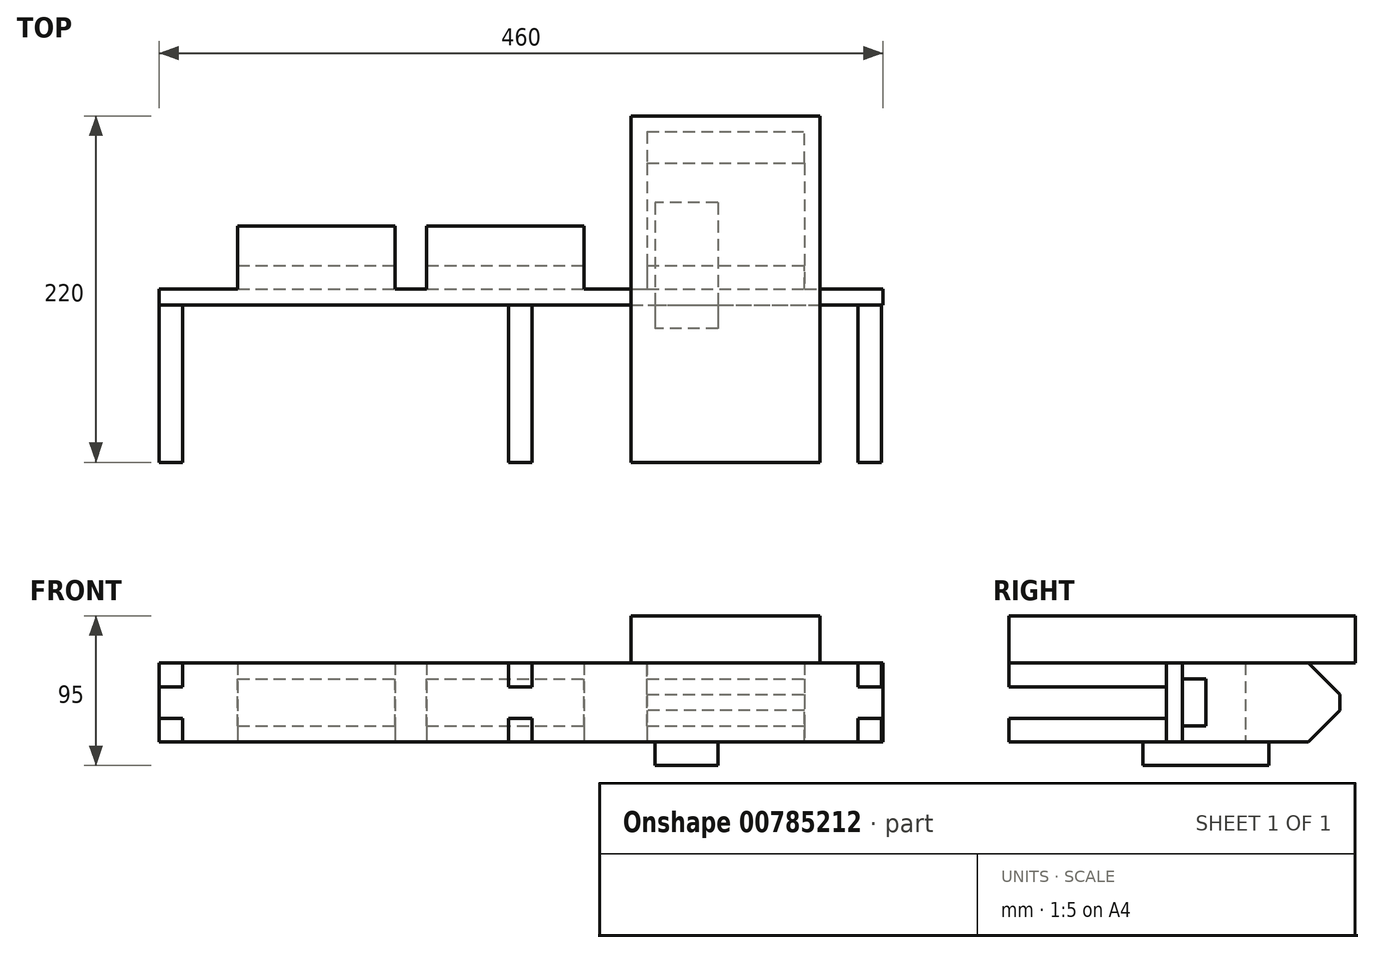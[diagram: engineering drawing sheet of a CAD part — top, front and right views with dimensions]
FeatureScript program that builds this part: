
annotation { "Feature Type Name" : "Feature", "Feature Type Description" : "" }
export const myFeature = defineFeature(function(context is Context, id is Id, definition is map)
    precondition{}
    {
        {
            var Q0;
            Q0=qCreatedBy(makeId("Front.planeOp"),FACE);
            var sketch = newSketch(context, id + "F0", { "sketchPlane" : qUnion([Q0])});
            skLineSegment(sketch, "E0.bottom", {"start": v(0, 0) * mm, "end": v(460, 0) * mm});
            skLineSegment(sketch, "E0.top", {"start": v(0, 50) * mm, "end": v(460, 50) * mm});
            skLineSegment(sketch, "E0.left", {"start": v(0, 0) * mm, "end": v(0, 50) * mm});
            skLineSegment(sketch, "E0.right", {"start": v(460, 0) * mm, "end": v(460, 50) * mm});
            skSolve(sketch);
        }
        {
            var Q0;
            Q0=makeQuery(id+"F0.imprint","IMPRINT",FACE,{"disambiguationData":[TD([[makeQuery(id+"F0.imprint","IMPRINT",EDGE,{"derivedFrom":sQuery(id+"F0.wireOp",EDGE,"E0.bottom")}),1.0]])]});
            extrude(context, id + "F1", {"entities" : qUnion([Q0]), "depth" : 10 * mm, "offsetDistance" : 25 * mm});
        }
        {
            var Q0;
            Q0=makeQuery(id+"F1.opExtrude","CAP_FACE",FACE,{"disambiguationData":[OSD([sQuery(id+"F0.wireOp",EDGE,"E0.bottom"),sQuery(id+"F0.wireOp",EDGE,"E0.top"),sQuery(id+"F0.wireOp",EDGE,"E0.left"),sQuery(id+"F0.wireOp",EDGE,"E0.right")])],"isStart":false});
            var sketch = newSketch(context, id + "F2", { "sketchPlane" : qUnion([Q0])});
            skLineSegment(sketch, "E1.bottom", {"start": v(0, 50) * mm, "end": v(15, 50) * mm});
            skLineSegment(sketch, "E1.top", {"start": v(0, 35) * mm, "end": v(15, 35) * mm});
            skLineSegment(sketch, "E1.left", {"start": v(0, 50) * mm, "end": v(0, 35) * mm});
            skLineSegment(sketch, "E1.right", {"start": v(15, 50) * mm, "end": v(15, 35) * mm});
            skLineSegment(sketch, "E2.bottom", {"start": v(0, 0) * mm, "end": v(15, 0) * mm});
            skLineSegment(sketch, "E2.top", {"start": v(0, 15) * mm, "end": v(15, 15) * mm});
            skLineSegment(sketch, "E2.left", {"start": v(0, 0) * mm, "end": v(0, 15) * mm});
            skLineSegment(sketch, "E2.right", {"start": v(15, 0) * mm, "end": v(15, 15) * mm});
            skLineSegment(sketch, "E3.1.0.0", {"start": v(222, 35) * mm, "end": v(237, 35) * mm});
            skLineSegment(sketch, "E3.1.0.1", {"start": v(222, 50) * mm, "end": v(237, 50) * mm});
            skLineSegment(sketch, "E3.1.0.2", {"start": v(222, 50) * mm, "end": v(222, 35) * mm});
            skLineSegment(sketch, "E3.1.0.3", {"start": v(237, 50) * mm, "end": v(237, 35) * mm});
            skLineSegment(sketch, "E3.1.0.4", {"start": v(222, 0) * mm, "end": v(237, 0) * mm});
            skLineSegment(sketch, "E3.1.0.5", {"start": v(222, 15) * mm, "end": v(237, 15) * mm});
            skLineSegment(sketch, "E3.1.0.6", {"start": v(222, 0) * mm, "end": v(222, 15) * mm});
            skLineSegment(sketch, "E3.1.0.7", {"start": v(237, 0) * mm, "end": v(237, 15) * mm});
            skLineSegment(sketch, "E3.2.0.0", {"start": v(444, 35) * mm, "end": v(459, 35) * mm});
            skLineSegment(sketch, "E3.2.0.1", {"start": v(444, 50) * mm, "end": v(459, 50) * mm});
            skLineSegment(sketch, "E3.2.0.2", {"start": v(444, 50) * mm, "end": v(444, 35) * mm});
            skLineSegment(sketch, "E3.2.0.3", {"start": v(459, 50) * mm, "end": v(459, 35) * mm});
            skLineSegment(sketch, "E3.2.0.4", {"start": v(444, 0) * mm, "end": v(459, 0) * mm});
            skLineSegment(sketch, "E3.2.0.5", {"start": v(444, 15) * mm, "end": v(459, 15) * mm});
            skLineSegment(sketch, "E3.2.0.6", {"start": v(444, 0) * mm, "end": v(444, 15) * mm});
            skLineSegment(sketch, "E3.2.0.7", {"start": v(459, 0) * mm, "end": v(459, 15) * mm});
            skLineSegment(sketch, "E3.direction1", {"start": v(0, 0) * mm, "end": v(222, 0) * mm, "construction": true});
            skSolve(sketch);
        }
        {
            var Q0;
            Q0=makeQuery(id+"F2.imprint","IMPRINT",FACE,{"disambiguationData":[TD([[makeQuery(id+"F2.imprint","IMPRINT",EDGE,{"derivedFrom":sQuery(id+"F2.wireOp",EDGE,"E1.bottom")}),-1.0]])]});
            var Q1;
            Q1=makeQuery(id+"F2.imprint","IMPRINT",FACE,{"disambiguationData":[TD([[makeQuery(id+"F2.imprint","IMPRINT",EDGE,{"derivedFrom":sQuery(id+"F2.wireOp",EDGE,"E2.bottom")}),1.0]])]});
            var Q2;
            Q2=makeQuery(id+"F2.imprint","IMPRINT",FACE,{"disambiguationData":[TD([[makeQuery(id+"F2.imprint","IMPRINT",EDGE,{"derivedFrom":sQuery(id+"F2.wireOp",EDGE,"E3.1.0.0")}),1.0]])]});
            var Q3;
            Q3=makeQuery(id+"F2.imprint","IMPRINT",FACE,{"disambiguationData":[TD([[makeQuery(id+"F2.imprint","IMPRINT",EDGE,{"derivedFrom":sQuery(id+"F2.wireOp",EDGE,"E3.1.0.4")}),1.0]])]});
            var Q4;
            Q4=makeQuery(id+"F2.imprint","IMPRINT",FACE,{"disambiguationData":[TD([[makeQuery(id+"F2.imprint","IMPRINT",EDGE,{"derivedFrom":sQuery(id+"F2.wireOp",EDGE,"E3.2.0.0")}),1.0]])]});
            var Q5;
            Q5=makeQuery(id+"F2.imprint","IMPRINT",FACE,{"disambiguationData":[TD([[makeQuery(id+"F2.imprint","IMPRINT",EDGE,{"derivedFrom":sQuery(id+"F2.wireOp",EDGE,"E3.2.0.4")}),1.0]])]});
            extrude(context, id + "F3", {"entities" : qUnion([Q0, Q1, Q2, Q3, Q4, Q5]), "depth" : 100 * mm, "offsetDistance" : 25 * mm});
        }
        {
            var Q0;
            Q0=makeQuery(id+"F1.opExtrude","CAP_FACE",FACE,{"disambiguationData":[OSD([sQuery(id+"F0.wireOp",EDGE,"E0.bottom"),sQuery(id+"F0.wireOp",EDGE,"E0.top"),sQuery(id+"F0.wireOp",EDGE,"E0.left"),sQuery(id+"F0.wireOp",EDGE,"E0.right")])],"isStart":true});
            var sketch = newSketch(context, id + "F4", { "sketchPlane" : qUnion([Q0])});
            skLineSegment(sketch, "E4.bottom", {"start": v(-410, 50) * mm, "end": v(-310, 50) * mm});
            skLineSegment(sketch, "E4.top", {"start": v(-410, 0) * mm, "end": v(-310, 0) * mm});
            skLineSegment(sketch, "E4.left", {"start": v(-410, 50) * mm, "end": v(-410, 0) * mm});
            skLineSegment(sketch, "E4.right", {"start": v(-310, 50) * mm, "end": v(-310, 0) * mm});
            skLineSegment(sketch, "E5.bottom", {"start": v(-270, 50) * mm, "end": v(-170, 50) * mm});
            skLineSegment(sketch, "E5.top", {"start": v(-270, 0) * mm, "end": v(-170, 0) * mm});
            skLineSegment(sketch, "E5.left", {"start": v(-270, 50) * mm, "end": v(-270, 0) * mm});
            skLineSegment(sketch, "E5.right", {"start": v(-170, 50) * mm, "end": v(-170, 0) * mm});
            skLineSegment(sketch, "E6.bottom", {"start": v(-150, 50) * mm, "end": v(-50, 50) * mm});
            skLineSegment(sketch, "E6.top", {"start": v(-150, 0) * mm, "end": v(-50, 0) * mm});
            skLineSegment(sketch, "E6.left", {"start": v(-150, 50) * mm, "end": v(-150, 0) * mm});
            skLineSegment(sketch, "E6.right", {"start": v(-50, 50) * mm, "end": v(-50, 0) * mm});
            skSolve(sketch);
        }
        {
            var Q0;
            Q0=makeQuery(id+"F4.imprint","IMPRINT",FACE,{"disambiguationData":[TD([[makeQuery(id+"F4.imprint","IMPRINT",EDGE,{"derivedFrom":sQuery(id+"F4.wireOp",EDGE,"E4.bottom")}),1.0]])]});
            var Q1;
            Q1=makeQuery(id+"F4.imprint","IMPRINT",FACE,{"disambiguationData":[TD([[makeQuery(id+"F4.imprint","IMPRINT",EDGE,{"derivedFrom":sQuery(id+"F4.wireOp",EDGE,"E5.bottom")}),1.0]])]});
            var Q2;
            Q2=makeQuery(id+"F4.imprint","IMPRINT",FACE,{"disambiguationData":[TD([[makeQuery(id+"F4.imprint","IMPRINT",EDGE,{"derivedFrom":sQuery(id+"F4.wireOp",EDGE,"E6.bottom")}),1.0]])]});
            extrude(context, id + "F5", {"entities" : qUnion([Q0, Q1, Q2]), "operationType" : NewBodyOperationType.ADD, "depth" : 40 * mm, "offsetDistance" : 25 * mm});
        }
        {
            var Q0;
            Q0=makeQuery(id+"F5.opExtrude","CAP_FACE",FACE,{"disambiguationData":[OSD([sQuery(id+"F4.wireOp",EDGE,"E4.bottom"),sQuery(id+"F4.wireOp",EDGE,"E4.top"),sQuery(id+"F4.wireOp",EDGE,"E4.left"),sQuery(id+"F4.wireOp",EDGE,"E4.right")])],"isStart":false});
            var sketch = newSketch(context, id + "F6", { "sketchPlane" : qUnion([Q0])});
            skLineSegment(sketch, "E7.bottom", {"start": v(-410, 50) * mm, "end": v(-310, 50) * mm});
            skLineSegment(sketch, "E7.top", {"start": v(-410, 0) * mm, "end": v(-310, 0) * mm});
            skLineSegment(sketch, "E7.left", {"start": v(-410, 50) * mm, "end": v(-410, 0) * mm});
            skLineSegment(sketch, "E7.right", {"start": v(-310, 50) * mm, "end": v(-310, 0) * mm});
            skSolve(sketch);
        }
        {
            var Q0;
            Q0=makeQuery(id+"F6.imprint","IMPRINT",FACE,{"disambiguationData":[TD([[makeQuery(id+"F6.imprint","IMPRINT",EDGE,{"derivedFrom":sQuery(id+"F6.wireOp",EDGE,"E7.bottom")}),1.0]])]});
            extrude(context, id + "F7", {"entities" : qUnion([Q0]), "operationType" : NewBodyOperationType.ADD, "depth" : 60 * mm, "offsetDistance" : 25 * mm});
        }
        {
            var Q0;
            Q0=makeQuery(id+"F7.opExtrude","CAP_EDGE",EDGE,{"disambiguationData":[OSD([sQuery(id+"F6.wireOp",EDGE,"E7.top")])],"isStart":false});
            var Q1;
            Q1=makeQuery(id+"F7.opExtrude","CAP_EDGE",EDGE,{"disambiguationData":[OSD([sQuery(id+"F6.wireOp",EDGE,"E7.bottom")])],"isStart":false});
            chamfer(context, id + "F8", {"entities" : qUnion([Q0, Q1]), "width" : 20 * mm, "tangentPropagation" : true});
        }
        {
            var Q0;
            Q0=makeQuery(id+"F7.boolean.opBoolean","MERGE",FACE,{"derivedFrom":[makeQuery(id+"F5.boolean.opBoolean","MERGE",FACE,{"derivedFrom":[makeQuery(id+"F1.opExtrude","SWEPT_FACE",FACE,{"disambiguationData":[OSD([sQuery(id+"F0.wireOp",EDGE,"E0.top")])]}),makeQuery(id+"F5.opExtrude","SWEPT_FACE",FACE,{"disambiguationData":[OSD([sQuery(id+"F4.wireOp",EDGE,"E4.bottom")])]}),makeQuery(id+"F5.opExtrude","SWEPT_FACE",FACE,{"disambiguationData":[OSD([sQuery(id+"F4.wireOp",EDGE,"E5.bottom")])]}),makeQuery(id+"F5.opExtrude","SWEPT_FACE",FACE,{"disambiguationData":[OSD([sQuery(id+"F4.wireOp",EDGE,"E6.bottom")])]})]}),makeQuery(id+"F7.opExtrude","SWEPT_FACE",FACE,{"disambiguationData":[OSD([sQuery(id+"F6.wireOp",EDGE,"E7.bottom")])]})]});
            var sketch = newSketch(context, id + "F9", { "sketchPlane" : qUnion([Q0])});
            skLineSegment(sketch, "E8.bottom", {"start": v(300, 110) * mm, "end": v(420, 110) * mm});
            skLineSegment(sketch, "E8.top", {"start": v(300, -110) * mm, "end": v(420, -110) * mm});
            skLineSegment(sketch, "E8.left", {"start": v(300, 110) * mm, "end": v(300, -110) * mm});
            skLineSegment(sketch, "E8.right", {"start": v(420, 110) * mm, "end": v(420, -110) * mm});
            skSolve(sketch);
        }
        {
            var Q0;
            {var subQ0=sQuery(id+"F9.wireOp",EDGE,"E8.top");Q0=makeQuery(id+"F9.imprint","IMPRINT",FACE,{"disambiguationData":[TD([[makeQuery(id+"F9.imprint","IMPRINT",EDGE,{"derivedFrom":subQ0}),1.0]])]});}
            var Q1;
            {var subQ1=sQuery(id+"F9.wireOp",EDGE,"E8.bottom");Q1=makeQuery(id+"F9.imprint","IMPRINT",FACE,{"disambiguationData":[TD([[makeQuery(id+"F9.imprint","IMPRINT",EDGE,{"derivedFrom":subQ1}),-1.0]])]});}
            var Q2;
            {var subQ5=sQuery(id+"F0.wireOp",EDGE,"E0.top");var subQ16=makeQuery(id+"F1.opExtrude","CAP_EDGE",EDGE,{"disambiguationData":[OSD([subQ5])],"isStart":false});var subQ18=sQuery(id+"F9.wireOp",EDGE,"E8.left");var subQ19=makeQuery(id+"F9.imprint","INTERSECT",VERTEX,{"derivedFrom":[subQ16,subQ18]});Q2=makeQuery(id+"F9.imprint","IMPRINT",FACE,{"disambiguationData":[TD([[makeQuery(id+"F9.imprint","IMPRINT",EDGE,{"disambiguationData":[TD([[subQ19,-1.0]])],"derivedFrom":subQ16}),1.0]])]});}
            extrude(context, id + "F10", {"entities" : qUnion([Q0, Q1, Q2]), "depth" : 30 * mm, "offsetDistance" : 25 * mm});
        }
        {
            var Q0;
            Q0=makeQuery(id+"F7.boolean.opBoolean","MERGE",FACE,{"derivedFrom":[makeQuery(id+"F5.boolean.opBoolean","MERGE",FACE,{"derivedFrom":[makeQuery(id+"F1.opExtrude","SWEPT_FACE",FACE,{"disambiguationData":[OSD([sQuery(id+"F0.wireOp",EDGE,"E0.bottom")])]}),makeQuery(id+"F5.opExtrude","SWEPT_FACE",FACE,{"disambiguationData":[OSD([sQuery(id+"F4.wireOp",EDGE,"E4.top")])]}),makeQuery(id+"F5.opExtrude","SWEPT_FACE",FACE,{"disambiguationData":[OSD([sQuery(id+"F4.wireOp",EDGE,"E5.top")])]}),makeQuery(id+"F5.opExtrude","SWEPT_FACE",FACE,{"disambiguationData":[OSD([sQuery(id+"F4.wireOp",EDGE,"E6.top")])]})]}),makeQuery(id+"F7.opExtrude","SWEPT_FACE",FACE,{"disambiguationData":[OSD([sQuery(id+"F6.wireOp",EDGE,"E7.top")])]})]});
            var sketch = newSketch(context, id + "F11", { "sketchPlane" : qUnion([Q0])});
            skLineSegment(sketch, "E9.bottom", {"start": v(355, -55) * mm, "end": v(315, -55) * mm});
            skLineSegment(sketch, "E9.top", {"start": v(355, 25) * mm, "end": v(315, 25) * mm});
            skLineSegment(sketch, "E9.left", {"start": v(355, -55) * mm, "end": v(355, 25) * mm});
            skLineSegment(sketch, "E9.right", {"start": v(315, -55) * mm, "end": v(315, 25) * mm});
            skSolve(sketch);
        }
        {
            var Q0;
            {var subQ0=sQuery(id+"F11.wireOp",EDGE,"E9.bottom");Q0=makeQuery(id+"F11.imprint","IMPRINT",FACE,{"disambiguationData":[TD([[makeQuery(id+"F11.imprint","IMPRINT",EDGE,{"derivedFrom":subQ0}),-1.0]])]});}
            var Q1;
            {var subQ0=sQuery(id+"F11.wireOp",EDGE,"E9.top");Q1=makeQuery(id+"F11.imprint","IMPRINT",FACE,{"disambiguationData":[TD([[makeQuery(id+"F11.imprint","IMPRINT",EDGE,{"derivedFrom":subQ0}),1.0]])]});}
            extrude(context, id + "F12", {"entities" : qUnion([Q0, Q1]), "operationType" : NewBodyOperationType.ADD, "depth" : 15 * mm, "offsetDistance" : 25 * mm});
        }
        {
            var Q0;
            Q0=makeQuery(id+"F7.boolean.opBoolean","MERGE",FACE,{"derivedFrom":[makeQuery(id+"F5.opExtrude","SWEPT_FACE",FACE,{"disambiguationData":[OSD([sQuery(id+"F4.wireOp",EDGE,"E4.left")])]}),makeQuery(id+"F7.opExtrude","SWEPT_FACE",FACE,{"disambiguationData":[OSD([sQuery(id+"F6.wireOp",EDGE,"E7.left")])]})]});
            var sketch = newSketch(context, id + "F13", { "sketchPlane" : qUnion([Q0])});
            skLineSegment(sketch, "E10.bottom", {"start": v(0, 40) * mm, "end": v(15, 40) * mm});
            skLineSegment(sketch, "E10.top", {"start": v(0, 10) * mm, "end": v(15, 10) * mm});
            skLineSegment(sketch, "E10.left", {"start": v(0, 40) * mm, "end": v(0, 10) * mm});
            skLineSegment(sketch, "E10.right", {"start": v(15, 40) * mm, "end": v(15, 10) * mm});
            skSolve(sketch);
        }
        {
            var Q0;
            Q0=makeQuery(id+"F13.imprint","IMPRINT",FACE,{"disambiguationData":[TD([[makeQuery(id+"F13.imprint","IMPRINT",EDGE,{"derivedFrom":sQuery(id+"F13.wireOp",EDGE,"E10.bottom")}),-1.0]])]});
            extrude(context, id + "F14", {"entities" : qUnion([Q0]), "operationType" : NewBodyOperationType.REMOVE, "oppositeDirection" : true, "depth" : 360.6 * mm, "offsetDistance" : 25 * mm});
        }
    });
